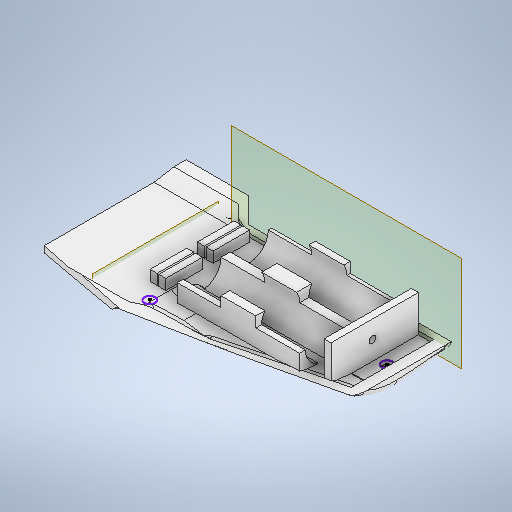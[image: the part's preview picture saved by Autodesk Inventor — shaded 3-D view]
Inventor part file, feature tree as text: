
AUTODESK INVENTOR PART (.ipt)
format: ipt  version: 2025 (Build 290162000, 162)  size: 3,510,784 bytes
history: native  units: in
note: dims shown in document units (in); Inventor stores cm internally (conversion verified against a paired STEP export)
features: extrude x44, sketch x37, fillet x33, other x28, reference x25, chamfer x10, projected_geometry x6, mirror x3, hole x1
ambient origin geometry x8: Origin, YZ Plane, XZ Plane, XY Plane, X Axis, Y Axis, Z Axis, Center Point
bodies: Body1 (feature_tree)
feature tree (187):
  other  "ソリッド1"
  sketch  "スケッチ1"
  extrude  "押し出し1"  Depth=3.3465in
  sketch  "スケッチ4"
  extrude  "押し出し4"  Depth=0.2756in
  extrude  "押し出し5"  Depth=9.8425in
  extrude  "押し出し6"  Depth=0.8661in TaperAngle=0.0deg
  extrude  "押し出し7"  Depth=0.8268in
  chamfer  "面取り1"  Distance=0.1181in
  chamfer  "面取り2"  Distance=0.1181in
  chamfer  "面取り3"  Distance=1.8504in
  chamfer  "面取り4"  Distance=1.1024in
  other  "作業平面3"
  other  "作業平面5"
  extrude  "押し出し8"  Depth=1.5354in
  other  "作業平面6"
  mirror  "ミラー1"
  chamfer  "面取り5"  Distance=3.3465in
  extrude  "押し出し9"  Depth=3.3465in TaperAngle=0.0deg
  fillet  "フィレット27"  Radius=3.3465in
  fillet  "フィレット28"  Radius=3.3465in
  fillet  "フィレット29"  Radius=0.1181in
  fillet  "フィレット30"  Radius=0.1181in
  fillet  "フィレット32"  Radius=0.1181in
  fillet  "フィレット35"  Radius=0.1181in
  fillet  "フィレット36"  Radius=0.3937in
  fillet  "フィレット37"  Radius=0.1575in
  fillet  "フィレット38"  Radius=0.7087in
  fillet  "フィレット42"  [1 undecoded]
  fillet  "フィレット43"  Radius=0.3543in
  fillet  "フィレット44"  Radius=1.9685in
  fillet  "フィレット45"  Radius=2.0866in
  other  "作業平面7"
  extrude  "押し出し10"  Depth=0.1969in
  fillet  "フィレット46"  Radius=0.1969in
  other  "作業平面8"
  extrude  "押し出し11"  Depth=0.7874in
  sketch  "スケッチ10"
  extrude  "押し出し12"  Depth=0.0787in
  extrude  "押し出し13"  Depth=0.3937in
  chamfer  "面取り6"  Distance=0.1181in
  sketch  "スケッチ11"
  chamfer  "面取り7"  Distance=0.1181in
  extrude  "押し出し14"  Depth=0.0354in
  chamfer  "面取り8"  Distance=0.0394in
  chamfer  "面取り9"  Distance=0.0787in
  extrude  "押し出し15"  Depth=0.0118in
  chamfer  "面取り10"  Distance=0.0354in
  other  "作業平面9"
  other  "作業平面10"
  extrude  "押し出し16"  [1 undecoded]
  fillet  "フィレット47"  Radius=0.0394in
  fillet  "フィレット48"  Radius=0.0394in
  fillet  "フィレット49"  Radius=0.0394in
  mirror  "ミラー7"
  mirror  "ミラー8"
  fillet  "フィレット58"  Radius=0.8268in
  fillet  "フィレット59"  Radius=0.0787in
  fillet  "フィレット60"  Radius=0.8268in
  fillet  "フィレット61"  Radius=1.1681in
  fillet  "フィレット62"  Radius=1.1681in
  fillet  "フィレット63"  Radius=0.6299in
  other  "作業平面11"
  extrude  "押し出し17"  TaperAngle=45.0deg  [1 undecoded]
  extrude  "押し出し18"  Depth=0.3937in
  extrude  "押し出し19"  Depth=1.1811in TaperAngle=0.0deg
  extrude  "押し出し20"  Depth=0.3543in TaperAngle=45.0deg
  other  "作業平面13"
  extrude  "押し出し21"  Depth=0.0787in
  fillet  "フィレット66"  Radius=0.1181in
  fillet  "フィレット67"  Radius=0.0709in
  extrude  "押し出し22"  Depth=0.0394in TaperAngle=45.0deg
  other  "作業平面14"
  extrude  "押し出し23"  Depth=0.0394in TaperAngle=45.0deg
  other  "作業平面15"
  extrude  "押し出し24"  Depth=0.0591in TaperAngle=0.0deg
  extrude  "押し出し25"  Depth=0.1969in TaperAngle=45.0deg
  other  "作業平面16"
  extrude  "押し出し26"  Depth=0.0591in TaperAngle=0.0deg
  extrude  "押し出し27"  Depth=3.937in
  other  "作業平面17"
  extrude  "押し出し28"  Depth=1.9685in
  extrude  "押し出し29"  Depth=0.1181in
  sketch  "スケッチ29"
  extrude  "押し出し30"  Depth=0.1181in
  extrude  "押し出し31"  Depth=0.0787in
  extrude  "押し出し32"  Depth=0.0197in
  extrude  "押し出し33"  Depth=0.0197in
  other  "作業平面18"
  extrude  "押し出し34"  Depth=0.3937in
  extrude  "押し出し35"  Depth=0.1181in
  fillet  "フィレット68"  [1 undecoded]
  fillet  "フィレット69"  Radius=1.1811in
  fillet  "フィレット70"  Radius=0.0787in
  fillet  "フィレット71"  Radius=0.1181in
  fillet  "フィレット72"  Radius=0.0197in
  extrude  "押し出し36"  Depth=0.0787in TaperAngle=0.0deg
  other  "作業平面19"
  fillet  "フィレット74"  Radius=0.9949in
  fillet  "フィレット75"  Radius=0.3937in
  fillet  "フィレット76"  Radius=0.0472in
  sketch  "スケッチ33"
  extrude  "押し出し39"  Depth=0.0669in
  extrude  "押し出し40"  Depth=0.0079in
  sketch  "スケッチ35"
  extrude  "押し出し41"  Depth=0.2756in
  other  "作業平面20"
  extrude  "押し出し42"  Depth=0.3543in
  sketch  "スケッチ37"
  extrude  "押し出し43"  Depth=0.3543in
  extrude  "押し出し44"  Depth=0.2756in
  sketch  "スケッチ38"
  hole  "穴2"  [1 undecoded]
  other  "作業平面21"
  sketch  "スケッチ40"
  extrude  "押し出し49"  Depth=0.0787in
  extrude  "押し出し50"  Depth=0.0079in
  extrude  "押し出し51"  Depth=0.1181in
  other  "作業平面22"
  extrude  "押し出し57"  Depth=0.0787in
  projected_geometry  "投影ループ2"
  sketch  "スケッチ5"
  projected_geometry  "投影ループ3"
  sketch  "スケッチ6"
  projected_geometry  "投影ループ4"
  other  "作業平面2"
  other  "作業平面4"
  sketch  "スケッチ7"
  sketch  "スケッチ8"
  projected_geometry  "投影ループ5"
  sketch  "スケッチ9"
  sketch  "スケッチ12"
  sketch  "スケッチ13"
  sketch  "スケッチ14"
  sketch  "スケッチ15"
  sketch  "スケッチ16"
  sketch  "スケッチ18"
  sketch  "スケッチ19"
  sketch  "スケッチ20"
  sketch  "スケッチ21"
  reference  "参照1"
  reference  "参照2"
  reference  "参照3"
  reference  "参照4"
  reference  "参照5"
  sketch  "スケッチ22"
  reference  "参照6"
  reference  "参照7"
  sketch  "スケッチ23"
  reference  "参照8"
  reference  "参照9"
  reference  "参照10"
  reference  "参照11"
  reference  "参照12"
  reference  "参照13"
  sketch  "スケッチ24"
  projected_geometry  "投影ループ6"
  sketch  "スケッチ25"
  sketch  "スケッチ26"
  sketch  "スケッチ27"
  sketch  "スケッチ28"
  reference  "参照14"
  reference  "参照15"
  other  "スケッチ円形状パターン1"
  sketch  "スケッチ30"
  reference  "参照16"
  sketch  "スケッチ31"
  reference  "参照17"
  reference  "参照18"
  reference  "参照19"
  reference  "参照21"
  reference  "参照22"
  reference  "参照23"
  reference  "参照24"
  reference  "参照25"
  reference  "参照29"
  sketch  "スケッチ32"
  sketch  "スケッチ34"
  sketch  "スケッチ36"
  projected_geometry  "投影ループ7"
  sketch  "スケッチ44"
  other  "<userpath>\OneDrive\ドキュメント\New Controller\Hardware\Assembly.iam"
  other  "Assembly.iam"
  other  "Nano33BLE:1"
  other  "Cuicuit:1"
  other  "switch:1"
  other  "mini vibrator:1"
note: 5 required parameter values undecoded (feature->parameter linkage not recoverable at this tier; creation-order binding heuristic only, values carry confidence <= 0.55)
